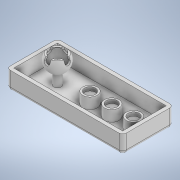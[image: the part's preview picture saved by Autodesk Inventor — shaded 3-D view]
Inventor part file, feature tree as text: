
AUTODESK INVENTOR PART (.ipt)
format: ipt  version: 2021 (Build 250183000, 183)  size: 289,792 bytes
history: native  units: in
note: dims shown in document units (in); Inventor stores cm internally (conversion verified against a paired STEP export)
features: sketch x9, extrude x8, fillet x2, revolve x1
ambient origin geometry x8: Origin, YZ Plane, XZ Plane, XY Plane, X Axis, Y Axis, Z Axis, Center Point
bodies: Solid1 (feature_tree)
feature tree (20):
  revolve  "Revolution1"  [1 undecoded]
  extrude  "Extrusion1"  TaperAngle=90.0deg  [1 undecoded]
  fillet  "Fillet1"  Radius=0.1476in
  extrude  "Extrusion2"  Depth=0.1476in
  extrude  "Extrusion3"  Depth=0.2953in TaperAngle=0.0deg
  extrude  "Extrusion4"  Depth=0.1476in
  extrude  "Extrusion5"  Depth=1.1811in
  extrude  "Extrusion6"  Depth=0.1969in TaperAngle=0.0deg
  extrude  "Extrusion7"  Depth=0.9843in
  extrude  "Extrusion8"  Depth=0.1969in TaperAngle=0.0deg
  fillet  "Fillet2"  Radius=0.1969in
  sketch  "Sketch1"  dims[d0=0.9843in d2=1.1811in]
  sketch  "Sketch2"  dims[d3=0.5906in d4=90.0deg d5=0.1476in]
  sketch  "Sketch3"  dims[d6=0.1476in d7=0.1476in]
  sketch  "Sketch4"  dims[d8=0.1476in d9=0.2953in d10=0.0in]
  sketch  "Sketch5"  dims[d11=0.1476in d12=1.1811in]
  sketch  "Sketch6"  dims[d13=1.1811in d14=1.1811in]
  sketch  "Sketch7"  dims[d15=4.7244in d16=0.1969in d17=0.0in]
  sketch  "Sketch8"  dims[d18=2.3622in d19=0.9843in]
  sketch  "Sketch9"  dims[d20=0.1969in d21=0.0in d22=0.1969in d23=0.0in d24=0.1969in d25=0.0in d27=1.1811in d29=1.1811in d30=1.1811in d31=2.3622in d32=0.7874in d33=0.5906in d34=0.0in d35=0.5906in d36=0.1969in d37=0.0in d38=0.1969in d39=0.0in d40=0.1969in]
note: 2 required parameter values undecoded (feature->parameter linkage not recoverable at this tier; creation-order binding heuristic only, values carry confidence <= 0.55)